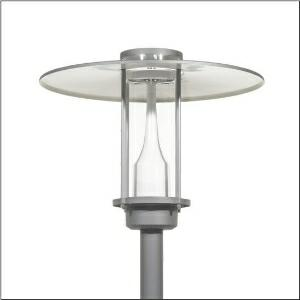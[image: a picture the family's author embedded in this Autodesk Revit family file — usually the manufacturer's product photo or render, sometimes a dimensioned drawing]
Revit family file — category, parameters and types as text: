
# Revit family: city-light_plus_iq___p1_0a_5xa5275lf14h_b1b0
name_source: partatom
category: Lighting Fixtures
units: mm (PartAtom-declared; Revit-internal decimal feet)

## family parameters
Cut with Voids When Loaded = No
Host = Face
Light Source = No
Part Type = Normal
Room Calculation Point = No
Round Connector Dimension = Use Diameter
Shared = No

## types (1)
- --- (1 x LED, 1440 lm, 10 W, 4000K)
    Apparent Load = 10 VA
    CIE Flux Codes = 32 61 90 96 100
    Color Rendering = 70
    Color Temperature = 4000K
    Default Elevation = 1800 mm
    Description = City-Light Plus iQ, mast luminaire, Module 540 iQ-SR, primary light control with 3 zone facetted reflector, of plastic, silver coated, highly specular, structured, primary optical cover: cover, of PMMA, transparent, light distribution: P1.0a, light emission: direct distribution, primary light characteristic: strongly asymmetric, installation type: post-top, LED, High Power LED, rated luminous flux: 1.440lm, luminous efficacy: 144lm/W, light colour: 740, colour temperature: 4000K, control gear: iQ Street-Remote, control: pre-setting: logarithmic dimming characteristic, Street-Remote, Auto-Match, Temp-Guard, Lumen-Switch, Night-Set, Smart-Wire, Light-Fading, Desk-Remote (wireless, voltage-free reading and setting of iQ features in the workshop via application-optimized NFC function/RFID function), optimised constant luminous flux control (CLO 2.0), with terminal, 6-pole, max. 2.5mm², mains connection: 230..240V, AC, 50/60Hz, start of lifetime: 10W, end of service life: 10W, reduction: 5W, luminaire housing, upper part, of glass-fibre reinforced polyester, coated, Siteco® metallic grey (DB 702S), diameter: 750mm, height: 590mm, spigot size: d x l = 76 x 70mm (post-top) | with reducer (optional accessory) 60 x 70mm, mounting height: 3..5m, post-top mast mounting element, of diecast aluminium, coated, Siteco® metallic grey (DB 702S), Module 540 iQ-SR, traffic white (RAL 9016), equipment: standard, protection rating (complete): IP65, insulation class (complete): insulation class II (safety insulation), certification: CE, ENEC, VDE, packaging unit: 1 piece

Light Distribution: P1.0a
    Height = 590 mm
    Lamp = 1 x LED
    Lamp Light Flux = 1440 lm
    Lamp Power = 10 W
    Lamp count = 1
    Length = 750 mm
    Luminous efficacy = 144 lm/W
    Manufacturer = Siteco
    ModVariant = No
    Model = 5XA5275LF14H
    Number of Poles = 1
    OnlyDefault = Yes
    Power Factor = 1
    Product Name = City-Light Plus iQ | P1.0a
    Product group = mast luminaire | pylon top
    ProductGroupID = 6100
    Protection Class = Protection class II
    Protection Degree = IP 65
    RLX_Detail_Level = 1
    RLX_Emergency_Light_Flux = 0 lm
    RLX_Emergency_Type = 0
    RLX_Emergency_Type_DB = No
    RlxData = <blob elided: 64869 chars, md5=f887285c>
    Socket = socket
    Standby Power = 0 W
    System Light Flux = 1440 lm
    System Power = 10 W
    Type Comments = factory setting: luminous flux: 100 % | dim-lin: 254 | 401 mA
    Type Image = l_1006456.jpg
    URL = http://relux.com
    VarID = @adj_159978
    Voltage = 0 V
    Weight = 0.00 kg
    Width = 0 mm  [stored 0 ft]

note: [stored X ft] marks values corroborated as IEEE doubles in the binary element streams (Revit-internal decimal feet)

## geometry (parser evidence)
native form markers: Blend x4, Sweep x11
no freeform markers — native parametric forms only
